# Revit family: HERZ Strömax Commissioning Valve With Test Points, Straight Body 4217 GM
name_source: partatom
category: Rohrzubehör
units: mm (PartAtom-declared; Revit-internal decimal feet)

## family parameters
Arbeitsebenenbasiert = Nein
Beim Laden mit Abzugskörper schneiden = Nein
Bemaßung runder Anschluss = Durchmesser verwenden
Gemeinsam genutzt = Nein
Immer vertikal = Ja
OmniClass-Nummer = 23.65.55.14
OmniClass-Titel = Valves for Liquid Services
Teiletyp = Unterbricht

## types (1)
- HERZ Strömax Commissioning Valve With Test Points, Straight Body 4217 GM
    Body = DZR brass
    D04 = 9 mm  [stored 0.0295276 ft]
    Differential pressure measurement = The STRÖMAX-GM commissioning valve is equipped with two test points.
The differential pressure can be measured using a suitable measuring instrument, which permits calculation of the flow rate as a function of the respective presetting step.
The HERZ-Measuring computer (1 8900 05) permits direct flow rate reading (consult the equipment manual).
    Field of application = For hydraulic balancing in heating and cooling systems, adjustment of distribution mains, circuits, heat exchangers, heating and cooling registers, etc.
    H03 = 10 mm  [stored 0.0328084 ft]
    Hersteller = HERZ Armaturen Ges.m.b.H.
    Installation position = The non-rising valve spindle arranged perpendicular to the valve axis guarantees optimum accessibility and optimum valve operation in any installation position.
    MD01 = 9.5 mm  [stored 0.031168 ft]
    Max. operating pressure = 1600000.0 Pa
    Max. operating temperature (from DN40) = 110 °C
    Max. operating temperature (up to DN32) = 130 °C
    Medium = Water purity in accordance with the OeNORM H5195 and VDI 2035 standards.
Ethylene and propylene glycol can be mixed to a ratio of 25 - 50 vol. [%].
    Model = STRÖMAX-GM commissioning valve with test points, 1/2′′ – 3′′:
Screw down model, brass version, socket x socket, non-rising spindle, spindle seal by means of double-O-ring, presetting by limitation of valve lift by means of internal spindle;
digital display of presetting step at the hand wheel window.
2 standard test points are located adjacent to the hand wheel.
    S02 = 60 mm  [stored 0.19685 ft]
    SCRNCODE = 05;07;02
    SCRNSEQ = ARM;ARM_TYP="STRV";2
    SC_NennweiteBerechnet = 0
    URL = www.herzvalves.com
    W01 = 30.00°
    W02 = 60.00°

note: [stored X ft] marks values corroborated as IEEE doubles in the binary element streams (Revit-internal decimal feet)
